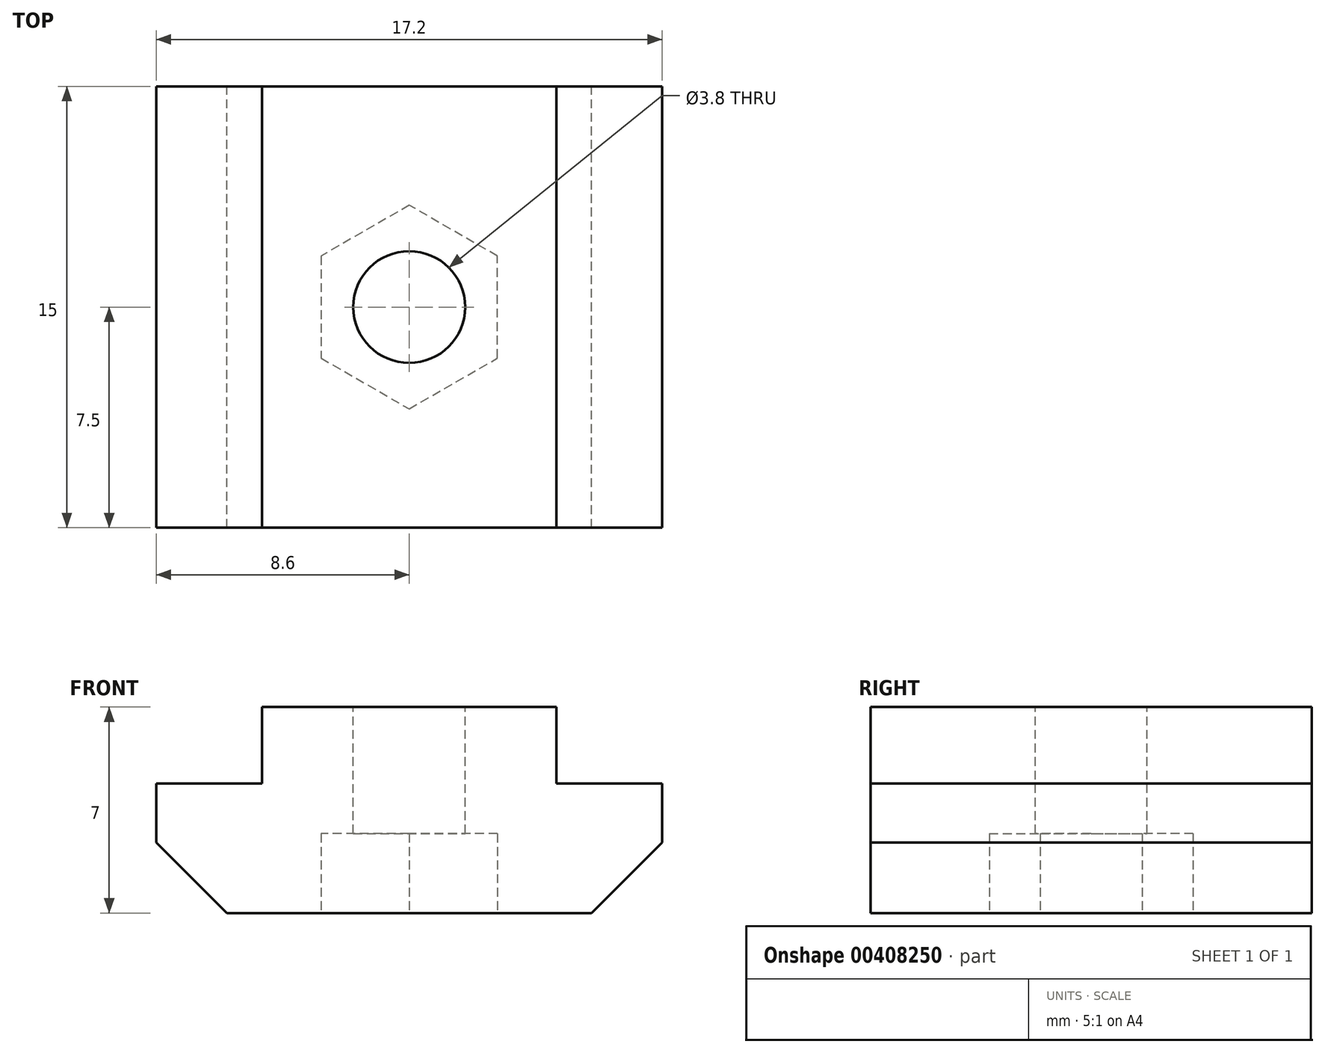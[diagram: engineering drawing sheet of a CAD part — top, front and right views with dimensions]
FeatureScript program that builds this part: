
annotation { "Feature Type Name" : "Feature", "Feature Type Description" : "" }
export const myFeature = defineFeature(function(context is Context, id is Id, definition is map)
    precondition{}
    {
        {
            var Q0;
            Q0=qCreatedBy(makeId("Front.planeOp"),FACE);
            var sketch = newSketch(context, id + "F0", { "sketchPlane" : qUnion([Q0])});
            skLineSegment(sketch, "E0", {"start": v(-8.6, 2.4) * mm, "end": v(-8.6, 4.4) * mm});
            skLineSegment(sketch, "E1", {"start": v(-8.6, 4.4) * mm, "end": v(-5, 4.4) * mm});
            skLineSegment(sketch, "E2", {"start": v(-5, 4.4) * mm, "end": v(-5, 7) * mm});
            skLineSegment(sketch, "E3", {"start": v(-5, 7) * mm, "end": v(0, 7) * mm});
            skLineSegment(sketch, "E4", {"start": v(0, 7) * mm, "end": v(0, 0) * mm});
            skLineSegment(sketch, "E5", {"start": v(-8.6, 2.4) * mm, "end": v(-6.2, 0) * mm});
            skLineSegment(sketch, "E6", {"start": v(-6.2, 0) * mm, "end": v(0, 0) * mm});
            skLineSegment(sketch, "E7.MirrorCS", {"start": v(5, 4.4) * mm, "end": v(5, 7) * mm});
            skLineSegment(sketch, "E8.MirrorCS", {"start": v(8.6, 2.4) * mm, "end": v(6.2, 0) * mm});
            skLineSegment(sketch, "E9.MirrorCS", {"start": v(8.6, 2.4) * mm, "end": v(8.6, 4.4) * mm});
            skLineSegment(sketch, "E10.MirrorCS", {"start": v(5, 7) * mm, "end": v(0, 7) * mm});
            skLineSegment(sketch, "E11.MirrorCS", {"start": v(8.6, 4.4) * mm, "end": v(5, 4.4) * mm});
            skLineSegment(sketch, "E12.MirrorCS", {"start": v(6.2, 0) * mm, "end": v(0, 0) * mm});
            skSolve(sketch);
        }
        {
            var Q0;
            Q0=makeQuery(id+"F0.imprint","IMPRINT",FACE,{"disambiguationData":[TD([[makeQuery(id+"F0.imprint","IMPRINT",EDGE,{"derivedFrom":sQuery(id+"F0.wireOp",EDGE,"E4")}),1.0]])]});
            var Q1;
            Q1=makeQuery(id+"F0.imprint","IMPRINT",FACE,{"disambiguationData":[TD([[makeQuery(id+"F0.imprint","IMPRINT",EDGE,{"derivedFrom":sQuery(id+"F0.wireOp",EDGE,"E0")}),-1.0]])]});
            extrude(context, id + "F1", {"entities" : qUnion([Q0, Q1]), "depth" : 15 * mm});
        }
        {
            var Q0;
            Q0=makeQuery(id+"F1.opExtrude","SWEPT_FACE",FACE,{"disambiguationData":[OSD([sQuery(id+"F0.wireOp",EDGE,"E3"),sQuery(id+"F0.wireOp",EDGE,"E10.MirrorCS")])]});
            var sketch = newSketch(context, id + "F2", { "sketchPlane" : qUnion([Q0])});
            skLineSegment(sketch, "E13", {"start": v(-5, 0) * mm, "end": v(5, -15) * mm, "construction": true});
            skPoint(sketch, "E14", {"position": v(0, -7.5) * mm});
            skSolve(sketch);
        }
        {
            var Q0;
            Q0=sQuery(id+"F2.wireOp",VERTEX,"E14");
            var Q1;
            Q1=makeQuery(id+"F1.opExtrude","SWEPT_BODY",BODY,{"disambiguationData":[OSD([sQuery(id+"F0.wireOp",EDGE,"E0"),sQuery(id+"F0.wireOp",EDGE,"E1"),sQuery(id+"F0.wireOp",EDGE,"E2"),sQuery(id+"F0.wireOp",EDGE,"E3"),sQuery(id+"F0.wireOp",EDGE,"E5"),sQuery(id+"F0.wireOp",EDGE,"E6"),sQuery(id+"F0.wireOp",EDGE,"E7.MirrorCS"),sQuery(id+"F0.wireOp",EDGE,"E8.MirrorCS"),sQuery(id+"F0.wireOp",EDGE,"E9.MirrorCS"),sQuery(id+"F0.wireOp",EDGE,"E10.MirrorCS"),sQuery(id+"F0.wireOp",EDGE,"E11.MirrorCS"),sQuery(id+"F0.wireOp",EDGE,"E12.MirrorCS")])]});
            hole(context, id + "F3", {"style" : HoleStyle.SIMPLE, "endStyle" : HoleEndStyle.THROUGH, "holeDiameter" : 3.8 * mm, "isTappedThrough" : true, "tappedDepth" : 12 * mm, "tapClearance" : 3, "locations" : qUnion([Q0]), "scope" : qUnion([Q1])});
        }
        {
            var Q0;
            Q0=makeQuery(id+"F1.opExtrude","SWEPT_FACE",FACE,{"disambiguationData":[OSD([sQuery(id+"F0.wireOp",EDGE,"E6"),sQuery(id+"F0.wireOp",EDGE,"E12.MirrorCS")])]});
            var sketch = newSketch(context, id + "F4", { "sketchPlane" : qUnion([Q0])});
            skCircle(sketch, "E15.cCircle", {"center": v(0, 7.5) * mm, "radius": 3 * mm, "construction": true});
            skLineSegment(sketch, "E15.0", {"start": v(0, 4.04) * mm, "end": v(-3, 5.77) * mm});
            skLineSegment(sketch, "E15.1", {"start": v(-3, 5.77) * mm, "end": v(-3, 9.23) * mm});
            skLineSegment(sketch, "E15.2", {"start": v(-3, 9.23) * mm, "end": v(0, 10.96) * mm});
            skLineSegment(sketch, "E15.3", {"start": v(0, 10.96) * mm, "end": v(3, 9.23) * mm});
            skLineSegment(sketch, "E15.4", {"start": v(3, 9.23) * mm, "end": v(3, 5.77) * mm});
            skLineSegment(sketch, "E15.5", {"start": v(3, 5.77) * mm, "end": v(0, 4.04) * mm});
            skPoint(sketch, "E15.0.midPoint", {"position": v(-1.5, 4.9) * mm});
            skSolve(sketch);
        }
        {
            var Q0;
            Q0=makeQuery(id+"F4.imprint","IMPRINT",FACE,{"disambiguationData":[TD([[makeQuery(id+"F4.imprint","IMPRINT",EDGE,{"derivedFrom":makeQuery(id+"F3.hole-0.boolean.opBoolean","INTERSECT",EDGE,{"derivedFrom":[makeQuery(id+"F1.opExtrude","SWEPT_FACE",FACE,{"disambiguationData":[OSD([sQuery(id+"F0.wireOp",EDGE,"E6"),sQuery(id+"F0.wireOp",EDGE,"E12.MirrorCS")])]}),makeQuery(id+"F3.hole-0.opRevolve","SWEPT_FACE",FACE,{"disambiguationData":[OSD([sQuery(id+"F3.hole-0.sketch.wireOp",EDGE,"core_line_2")])]})]})}),-1.0]])]});
            var Q1;
            Q1=makeQuery(id+"F4.imprint","IMPRINT",FACE,{"disambiguationData":[TD([[makeQuery(id+"F4.imprint","IMPRINT",EDGE,{"derivedFrom":sQuery(id+"F4.wireOp",EDGE,"E15.0")}),-1.0]])]});
            extrude(context, id + "F5", {"entities" : qUnion([Q0, Q1]), "operationType" : NewBodyOperationType.REMOVE, "oppositeDirection" : true, "depth" : 2.7 * mm});
        }
    });
